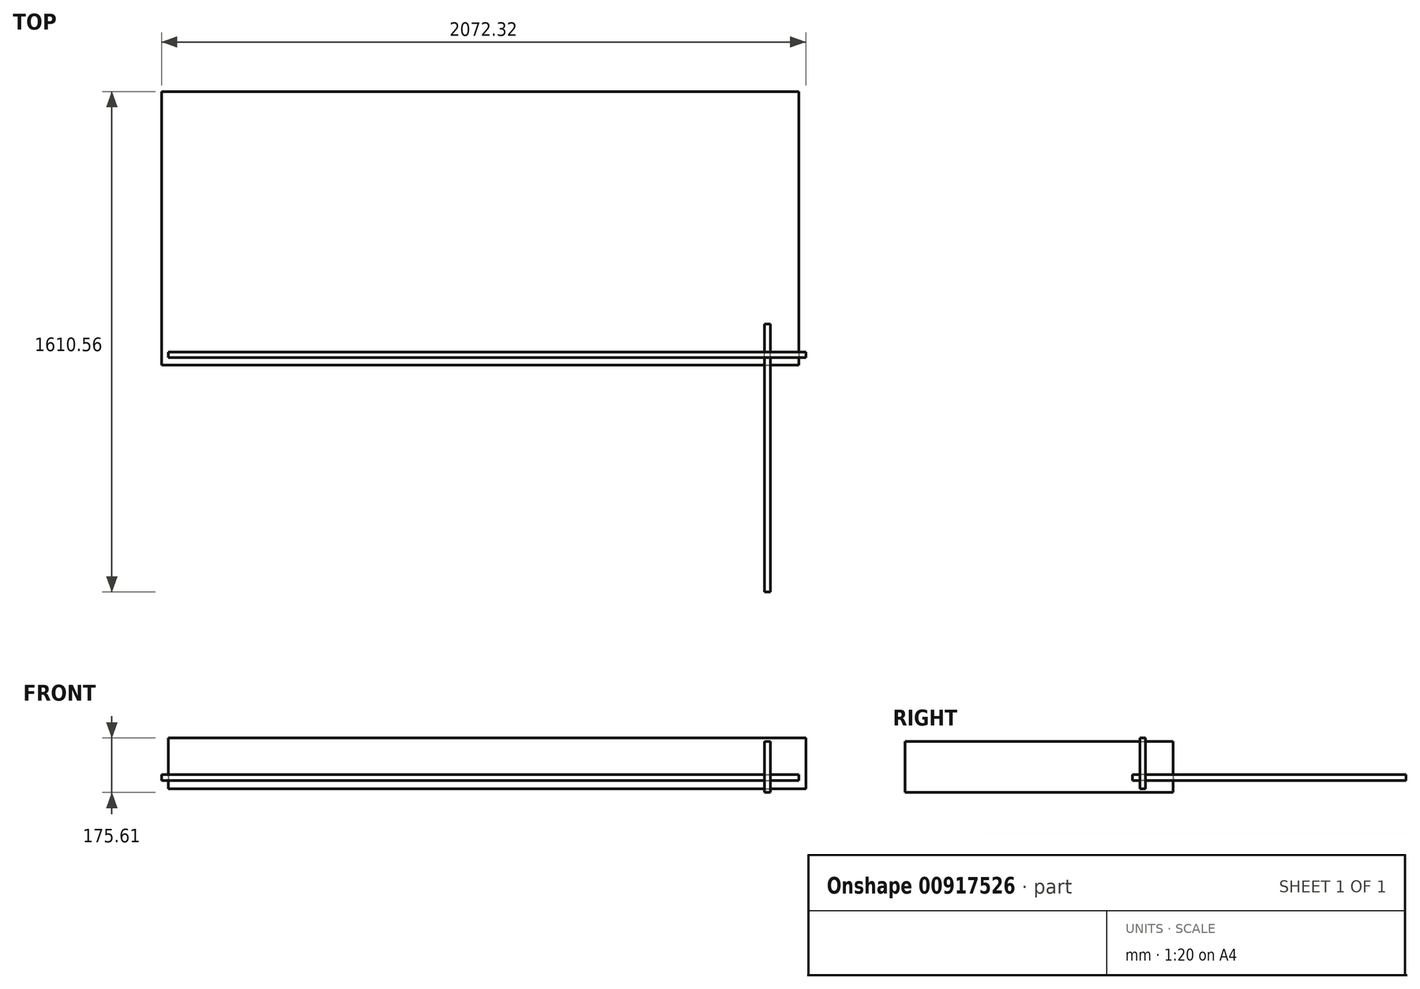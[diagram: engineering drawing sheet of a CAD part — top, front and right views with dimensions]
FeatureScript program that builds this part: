
annotation { "Feature Type Name" : "Feature", "Feature Type Description" : "" }
export const myFeature = defineFeature(function(context is Context, id is Id, definition is map)
    precondition{}
    {
        {
            var Q0;
            Q0=qCreatedBy(makeId("Top.planeOp"),FACE);
            var sketch = newSketch(context, id + "F0", { "sketchPlane" : qUnion([Q0])});
            skLineSegment(sketch, "E0.bottom", {"start": v(-1940.03, 837.81) * mm, "end": v(109.97, 837.81) * mm});
            skLineSegment(sketch, "E0.top", {"start": v(-1940.03, -42.19) * mm, "end": v(109.97, -42.19) * mm});
            skLineSegment(sketch, "E0.left", {"start": v(-1940.03, 837.81) * mm, "end": v(-1940.03, -42.19) * mm});
            skLineSegment(sketch, "E0.right", {"start": v(109.97, 837.81) * mm, "end": v(109.97, -42.19) * mm});
            skSolve(sketch);
        }
        {
            var Q0;
            Q0=qSketchRegion(id+"F0",true);
            extrude(context, id + "F1", {"entities" : qUnion([Q0]), "depth" : 18 * mm, "offsetDistance" : 25 * mm});
        }
        {
            var Q0;
            Q0=qCreatedBy(makeId("Front.planeOp"),FACE);
            var sketch = newSketch(context, id + "F2", { "sketchPlane" : qUnion([Q0])});
            skLineSegment(sketch, "E1.bottom", {"start": v(-1917.71, 136.51) * mm, "end": v(132.29, 136.51) * mm});
            skLineSegment(sketch, "E1.top", {"start": v(-1917.71, -27.49) * mm, "end": v(132.29, -27.49) * mm});
            skLineSegment(sketch, "E1.left", {"start": v(-1917.71, 136.51) * mm, "end": v(-1917.71, -27.49) * mm});
            skLineSegment(sketch, "E1.right", {"start": v(132.29, 136.51) * mm, "end": v(132.29, -27.49) * mm});
            skSolve(sketch);
        }
        {
            var Q0;
            Q0=qSketchRegion(id+"F2",true);
            extrude(context, id + "F3", {"entities" : qUnion([Q0]), "depth" : 18 * mm, "offsetDistance" : 25 * mm});
        }
        {
            var Q0;
            Q0=qCreatedBy(makeId("Right.planeOp"),FACE);
            var sketch = newSketch(context, id + "F4", { "sketchPlane" : qUnion([Q0])});
            skLineSegment(sketch, "E2.bottom", {"start": v(-772.75, 124.9) * mm, "end": v(89.25, 124.9) * mm});
            skLineSegment(sketch, "E2.top", {"start": v(-772.75, -39.1) * mm, "end": v(89.25, -39.1) * mm});
            skLineSegment(sketch, "E2.left", {"start": v(-772.75, 124.9) * mm, "end": v(-772.75, -39.1) * mm});
            skLineSegment(sketch, "E2.right", {"start": v(89.25, 124.9) * mm, "end": v(89.25, -39.1) * mm});
            skSolve(sketch);
        }
        {
            var Q0;
            Q0=qSketchRegion(id+"F4",true);
            extrude(context, id + "F5", {"entities" : qUnion([Q0]), "depth" : 18 * mm, "offsetDistance" : 25 * mm});
        }
    });
